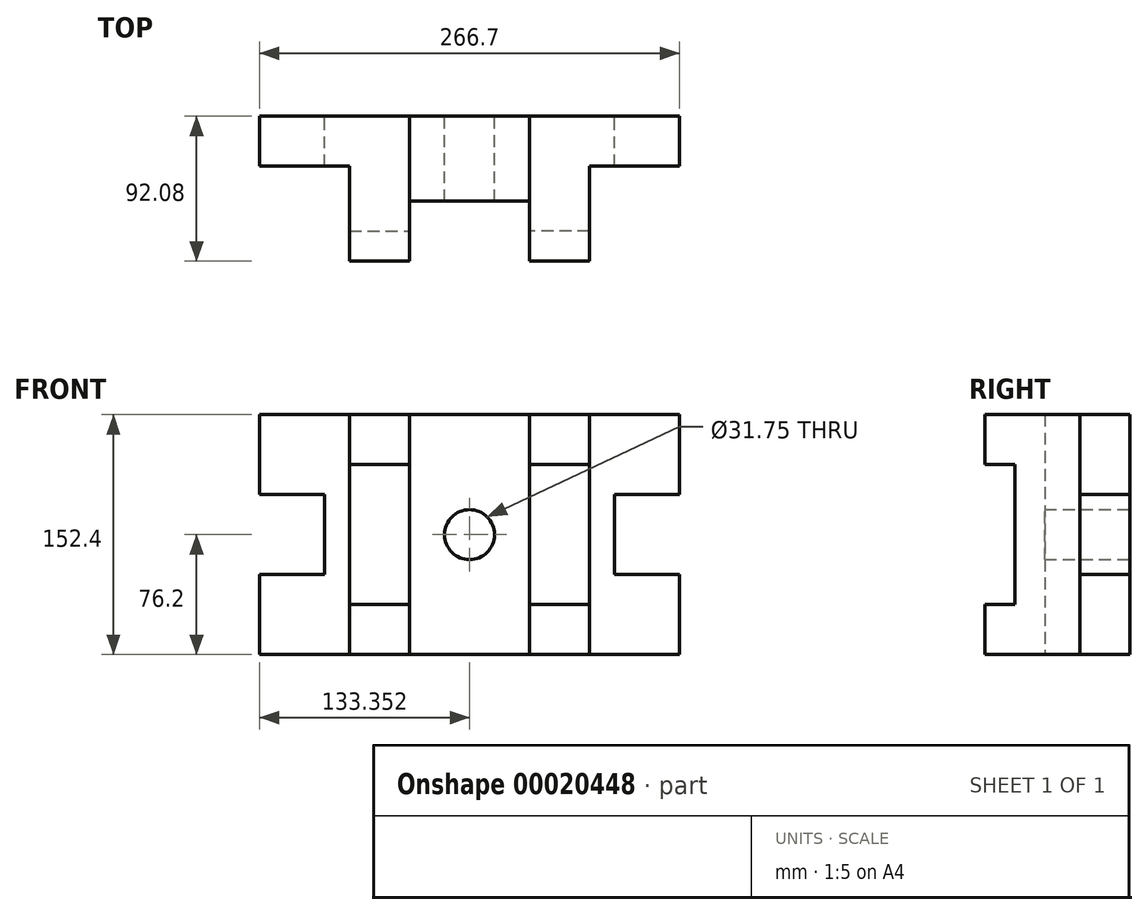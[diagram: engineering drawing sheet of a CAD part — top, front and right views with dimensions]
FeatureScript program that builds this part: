
annotation { "Feature Type Name" : "Feature", "Feature Type Description" : "" }
export const myFeature = defineFeature(function(context is Context, id is Id, definition is map)
    precondition{}
    {
        {
            var Q0;
            Q0=qCreatedBy(makeId("Front.planeOp"),FACE);
            var sketch = newSketch(context, id + "F0", { "sketchPlane" : qUnion([Q0])});
            skLineSegment(sketch, "E0", {"start": v(90.8, 101.6) * mm, "end": v(90.8, 50.8) * mm});
            skLineSegment(sketch, "E1", {"start": v(90.8, 50.8) * mm, "end": v(49.52, 50.8) * mm});
            skLineSegment(sketch, "E2", {"start": v(49.52, 50.8) * mm, "end": v(49.52, 0) * mm});
            skLineSegment(sketch, "E3", {"start": v(49.52, 0) * mm, "end": v(90.8, 0) * mm});
            skLineSegment(sketch, "E4", {"start": v(90.8, 0) * mm, "end": v(90.8, -50.8) * mm});
            skLineSegment(sketch, "E5", {"start": v(90.8, -50.8) * mm, "end": v(33.64, -50.8) * mm});
            skLineSegment(sketch, "E6", {"start": v(-42.56, 101.6) * mm, "end": v(-4.46, 101.6) * mm});
            skLineSegment(sketch, "E7", {"start": v(-4.46, 69.85) * mm, "end": v(-4.46, -19.05) * mm});
            skLineSegment(sketch, "E8", {"start": v(33.64, 101.6) * mm, "end": v(33.64, -50.8) * mm});
            skLineSegment(sketch, "E9", {"start": v(33.64, -19.05) * mm, "end": v(-4.46, -19.05) * mm});
            skLineSegment(sketch, "E10", {"start": v(33.64, 69.85) * mm, "end": v(-4.46, 69.85) * mm});
            skLineSegment(sketch, "E11.trimOffspring", {"start": v(33.64, 101.6) * mm, "end": v(90.8, 101.6) * mm});
            skLineSegment(sketch, "E12", {"start": v(-4.46, 101.6) * mm, "end": v(-4.46, 69.85) * mm});
            skLineSegment(sketch, "E13.trimOffspring", {"start": v(-4.46, -50.8) * mm, "end": v(-42.56, -50.8) * mm});
            skLineSegment(sketch, "E14", {"start": v(-4.46, -19.05) * mm, "end": v(-4.46, -50.8) * mm});
            skLineSegment(sketch, "E15", {"start": v(-4.46, 101.6) * mm, "end": v(33.64, 101.6) * mm});
            skLineSegment(sketch, "E16", {"start": v(-4.46, -50.8) * mm, "end": v(33.64, -50.8) * mm});
            skLineSegment(sketch, "E17.MirrorCS", {"start": v(-80.66, 69.85) * mm, "end": v(-80.66, -19.05) * mm});
            skLineSegment(sketch, "E18.MirrorCS", {"start": v(-80.66, -19.05) * mm, "end": v(-80.66, -50.8) * mm});
            skLineSegment(sketch, "E19.MirrorCS", {"start": v(-80.66, -50.8) * mm, "end": v(-42.56, -50.8) * mm});
            skLineSegment(sketch, "E20.MirrorCS", {"start": v(-42.56, 101.6) * mm, "end": v(-80.66, 101.6) * mm});
            skLineSegment(sketch, "E21.MirrorCS", {"start": v(-80.66, 101.6) * mm, "end": v(-118.76, 101.6) * mm});
            skLineSegment(sketch, "E22.MirrorCS", {"start": v(-118.76, 101.6) * mm, "end": v(-118.76, -50.8) * mm});
            skLineSegment(sketch, "E23.MirrorCS", {"start": v(-80.66, 101.6) * mm, "end": v(-80.66, 69.85) * mm});
            skLineSegment(sketch, "E24.MirrorCS", {"start": v(-118.76, 69.85) * mm, "end": v(-80.66, 69.85) * mm});
            skLineSegment(sketch, "E25.MirrorCS", {"start": v(-118.76, -19.05) * mm, "end": v(-80.66, -19.05) * mm});
            skLineSegment(sketch, "E26.MirrorCS", {"start": v(-80.66, -50.8) * mm, "end": v(-118.76, -50.8) * mm});
            skLineSegment(sketch, "E27.MirrorCS", {"start": v(-175.9, -50.8) * mm, "end": v(-118.76, -50.8) * mm});
            skLineSegment(sketch, "E28.MirrorCS", {"start": v(-175.9, 0) * mm, "end": v(-175.9, -50.8) * mm});
            skLineSegment(sketch, "E29.MirrorCS", {"start": v(-134.63, 0) * mm, "end": v(-175.9, 0) * mm});
            skLineSegment(sketch, "E30.MirrorCS", {"start": v(-134.63, 50.8) * mm, "end": v(-134.63, 0) * mm});
            skLineSegment(sketch, "E31.MirrorCS", {"start": v(-175.9, 50.8) * mm, "end": v(-134.63, 50.8) * mm});
            skLineSegment(sketch, "E32.MirrorCS", {"start": v(-175.9, 101.6) * mm, "end": v(-175.9, 50.8) * mm});
            skLineSegment(sketch, "E33.MirrorCS", {"start": v(-118.76, 101.6) * mm, "end": v(-175.9, 101.6) * mm});
            skCircle(sketch, "E34", {"center": v(-42.56, 25.4) * mm, "radius": 15.88 * mm});
            skSolve(sketch);
        }
        {
            var Q0;
            {var subQ1=sQuery(id+"F0.wireOp",EDGE,"E27.MirrorCS");Q0=makeQuery(id+"F0.imprint","IMPRINT",FACE,{"disambiguationData":[TD([[makeQuery(id+"F0.imprint","IMPRINT",EDGE,{"derivedFrom":subQ1}),1.0]])]});}
            extrude(context, id + "F1", {"entities" : qUnion([Q0]), "depth" : 31.75 * mm});
        }
        {
            var Q0;
            Q0=makeQuery(id+"F0.imprint","IMPRINT",FACE,{"disambiguationData":[TD([[makeQuery(id+"F0.imprint","IMPRINT",EDGE,{"derivedFrom":sQuery(id+"F0.wireOp",EDGE,"E0")}),-1.0]])]});
            extrude(context, id + "F2", {"entities" : qUnion([Q0]), "depth" : 31.75 * mm});
        }
        {
            var Q0;
            {var subQ2=sQuery(id+"F0.wireOp",EDGE,"E21.MirrorCS");Q0=makeQuery(id+"F0.imprint","IMPRINT",FACE,{"disambiguationData":[TD([[makeQuery(id+"F0.imprint","IMPRINT",EDGE,{"derivedFrom":subQ2}),1.0]])]});}
            extrude(context, id + "F3", {"entities" : qUnion([Q0]), "operationType" : NewBodyOperationType.ADD, "depth" : 92.07 * mm});
        }
        {
            var Q0;
            Q0=makeQuery(id+"F0.imprint","IMPRINT",FACE,{"disambiguationData":[TD([[makeQuery(id+"F0.imprint","IMPRINT",EDGE,{"derivedFrom":sQuery(id+"F0.wireOp",EDGE,"E18.MirrorCS")}),-1.0]])]});
            extrude(context, id + "F4", {"entities" : qUnion([Q0]), "operationType" : NewBodyOperationType.ADD, "depth" : 92.07 * mm});
        }
        {
            var Q0;
            {var subQ1=sQuery(id+"F0.wireOp",EDGE,"E10");Q0=makeQuery(id+"F0.imprint","IMPRINT",FACE,{"disambiguationData":[TD([[makeQuery(id+"F0.imprint","IMPRINT",EDGE,{"derivedFrom":subQ1}),-1.0]])]});}
            extrude(context, id + "F5", {"entities" : qUnion([Q0]), "operationType" : NewBodyOperationType.ADD, "depth" : 92.07 * mm});
        }
        {
            var Q0;
            {var subQ1=sQuery(id+"F0.wireOp",EDGE,"E9");Q0=makeQuery(id+"F0.imprint","IMPRINT",FACE,{"disambiguationData":[TD([[makeQuery(id+"F0.imprint","IMPRINT",EDGE,{"derivedFrom":subQ1}),1.0]])]});}
            extrude(context, id + "F6", {"entities" : qUnion([Q0]), "operationType" : NewBodyOperationType.ADD, "depth" : 92.07 * mm});
        }
        {
            var Q0;
            Q0=makeQuery(id+"F0.imprint","IMPRINT",FACE,{"disambiguationData":[TD([[makeQuery(id+"F0.imprint","IMPRINT",EDGE,{"derivedFrom":sQuery(id+"F0.wireOp",EDGE,"E17.MirrorCS")}),-1.0]])]});
            extrude(context, id + "F7", {"entities" : qUnion([Q0]), "operationType" : NewBodyOperationType.ADD, "depth" : 73.02 * mm});
        }
        {
            var Q0;
            Q0=makeQuery(id+"F0.imprint","IMPRINT",FACE,{"disambiguationData":[TD([[makeQuery(id+"F0.imprint","IMPRINT",EDGE,{"derivedFrom":sQuery(id+"F0.wireOp",EDGE,"E7")}),1.0]])]});
            extrude(context, id + "F8", {"entities" : qUnion([Q0]), "operationType" : NewBodyOperationType.ADD, "depth" : 73.02 * mm});
        }
        {
            var Q0;
            Q0=makeQuery(id+"F0.imprint","IMPRINT",FACE,{"disambiguationData":[TD([[makeQuery(id+"F0.imprint","IMPRINT",EDGE,{"derivedFrom":sQuery(id+"F0.wireOp",EDGE,"E6")}),-1.0]])]});
            extrude(context, id + "F9", {"entities" : qUnion([Q0]), "depth" : 53.97 * mm});
        }
    });
